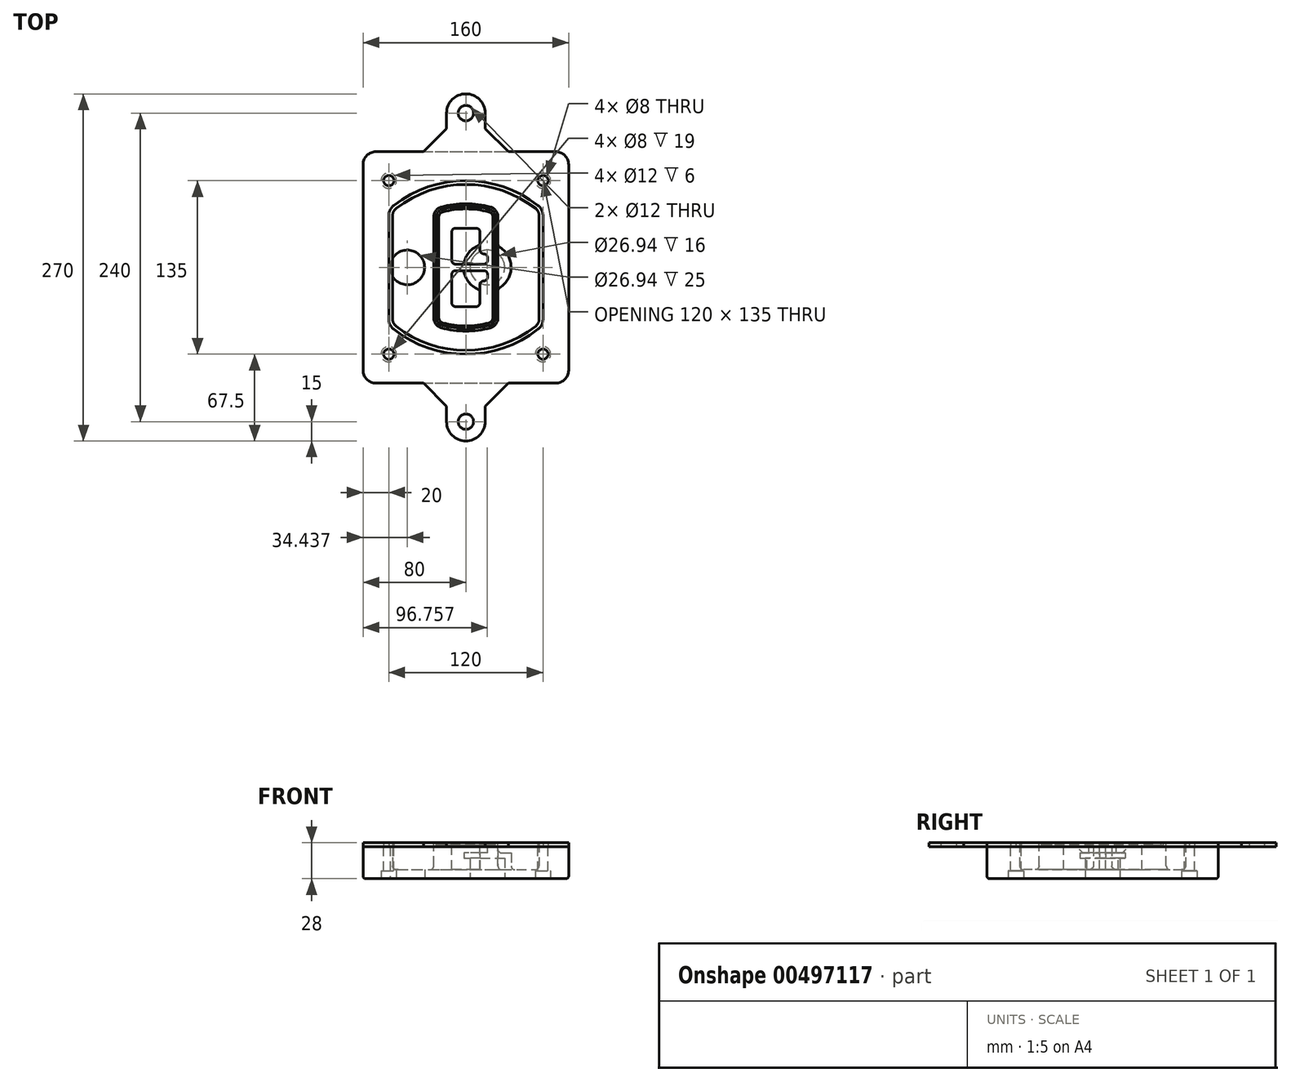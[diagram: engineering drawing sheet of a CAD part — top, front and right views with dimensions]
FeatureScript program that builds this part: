
annotation { "Feature Type Name" : "Feature", "Feature Type Description" : "" }
export const myFeature = defineFeature(function(context is Context, id is Id, definition is map)
    precondition{}
    {
        {
            var Q0;
            Q0=qCreatedBy(makeId("Top.planeOp"),FACE);
            var sketch = newSketch(context, id + "F0", { "sketchPlane" : qUnion([Q0])});
            skPoint(sketch, "E0.rect.middle", {"position": v(0, 0) * mm});
            skLineSegment(sketch, "E1.bottom", {"start": v(-70, -90) * mm, "end": v(70, -90) * mm});
            skLineSegment(sketch, "E1.top", {"start": v(-70, 90) * mm, "end": v(70, 90) * mm});
            skLineSegment(sketch, "E1.left", {"start": v(-80, -80) * mm, "end": v(-80, 80) * mm});
            skLineSegment(sketch, "E1.right", {"start": v(80, -80) * mm, "end": v(80, 80) * mm});
            skLineSegment(sketch, "E2", {"start": v(-80, 90) * mm, "end": v(80, -90) * mm, "construction": true});
            skLineSegment(sketch, "E3", {"start": v(80, 90) * mm, "end": v(-80, -90) * mm, "construction": true});
            skCircle(sketch, "E4", {"center": v(-60, 67.5) * mm, "radius": 4 * mm});
            skCircle(sketch, "E5", {"center": v(60, 67.5) * mm, "radius": 4 * mm});
            skCircle(sketch, "E6", {"center": v(60, -67.5) * mm, "radius": 4 * mm});
            skCircle(sketch, "E7", {"center": v(-60, -67.5) * mm, "radius": 4 * mm});
            skLineSegment(sketch, "E8", {"start": v(-60, 67.5) * mm, "end": v(60, 67.5) * mm, "construction": true});
            skLineSegment(sketch, "E9", {"start": v(60, 67.5) * mm, "end": v(60, -67.5) * mm, "construction": true});
            skLineSegment(sketch, "E10", {"start": v(60, -67.5) * mm, "end": v(-60, -67.5) * mm, "construction": true});
            skLineSegment(sketch, "E11", {"start": v(-60, -67.5) * mm, "end": v(-60, 67.5) * mm, "construction": true});
            skLineSegment(sketch, "E12", {"start": v(-60, 40.3) * mm, "end": v(-60, -40.3) * mm});
            skLineSegment(sketch, "E13", {"start": v(60, 40.3) * mm, "end": v(60, -40.3) * mm});
            skArc(sketch, "E14", {"start": v(56.15, 48.18) * mm, "mid": v(0, 67.5) * mm, "end": v(-56.15, 48.18) * mm});
            skArc(sketch, "E15", {"start": v(-56.15, -48.18) * mm, "mid": v(0, -67.5) * mm, "end": v(56.15, -48.18) * mm});
            skLineSegment(sketch, "E16", {"start": v(-60, 0) * mm, "end": v(60, 0) * mm, "construction": true});
            skPoint(sketch, "E17.visualSharp", {"position": v(-60, -45) * mm});
            skArc(sketch, "E17.filletArc", {"start": v(-60, -40.3) * mm, "mid": v(-58.99, -44.68) * mm, "end": v(-56.15, -48.18) * mm});
            skPoint(sketch, "E18.visualSharp", {"position": v(-60, 45) * mm});
            skArc(sketch, "E18.filletArc", {"start": v(-56.15, 48.18) * mm, "mid": v(-58.99, 44.68) * mm, "end": v(-60, 40.3) * mm});
            skPoint(sketch, "E19.visualSharp", {"position": v(60, 45) * mm});
            skArc(sketch, "E19.filletArc", {"start": v(60, 40.3) * mm, "mid": v(58.99, 44.68) * mm, "end": v(56.15, 48.18) * mm});
            skPoint(sketch, "E20.visualSharp", {"position": v(60, -45) * mm});
            skArc(sketch, "E20.filletArc", {"start": v(56.15, -48.18) * mm, "mid": v(58.99, -44.68) * mm, "end": v(60, -40.3) * mm});
            skPoint(sketch, "E21.visualSharp", {"position": v(-80, 90) * mm});
            skArc(sketch, "E21.filletArc", {"start": v(-70, 90) * mm, "mid": v(-77.07, 87.07) * mm, "end": v(-80, 80) * mm});
            skPoint(sketch, "E22.visualSharp", {"position": v(80, 90) * mm});
            skArc(sketch, "E22.filletArc", {"start": v(80, 80) * mm, "mid": v(77.07, 87.07) * mm, "end": v(70, 90) * mm});
            skPoint(sketch, "E23.visualSharp", {"position": v(80, -90) * mm});
            skArc(sketch, "E23.filletArc", {"start": v(70, -90) * mm, "mid": v(77.07, -87.07) * mm, "end": v(80, -80) * mm});
            skPoint(sketch, "E24.visualSharp", {"position": v(-80, -90) * mm});
            skArc(sketch, "E24.filletArc", {"start": v(-80, -80) * mm, "mid": v(-77.07, -87.07) * mm, "end": v(-70, -90) * mm});
            skArc(sketch, "E25.0", {"start": v(57, 40.3) * mm, "mid": v(56.3, 43.36) * mm, "end": v(54.3, 45.81) * mm});
            skLineSegment(sketch, "E25.1", {"start": v(57, 40.3) * mm, "end": v(57, -40.3) * mm});
            skArc(sketch, "E25.2", {"start": v(54.3, -45.81) * mm, "mid": v(56.3, -43.36) * mm, "end": v(57, -40.3) * mm});
            skArc(sketch, "E25.3", {"start": v(-54.3, -45.81) * mm, "mid": v(0, -64.5) * mm, "end": v(54.3, -45.81) * mm});
            skArc(sketch, "E25.4", {"start": v(-57, -40.3) * mm, "mid": v(-56.3, -43.36) * mm, "end": v(-54.3, -45.81) * mm});
            skArc(sketch, "E25.5", {"start": v(54.3, 45.81) * mm, "mid": v(0, 64.5) * mm, "end": v(-54.3, 45.81) * mm});
            skLineSegment(sketch, "E25.6", {"start": v(-57, 40.3) * mm, "end": v(-57, -40.3) * mm});
            skArc(sketch, "E25.7", {"start": v(-54.3, 45.81) * mm, "mid": v(-56.3, 43.36) * mm, "end": v(-57, 40.3) * mm});
            skArc(sketch, "E26.0", {"start": v(-58.62, 51.33) * mm, "mid": v(-62.58, 46.43) * mm, "end": v(-64, 40.3) * mm});
            skArc(sketch, "E26.1", {"start": v(58.62, 51.33) * mm, "mid": v(0, 71.5) * mm, "end": v(-58.62, 51.33) * mm});
            skArc(sketch, "E26.2", {"start": v(64, 40.3) * mm, "mid": v(62.58, 46.43) * mm, "end": v(58.62, 51.33) * mm});
            skLineSegment(sketch, "E26.3", {"start": v(64, 40.3) * mm, "end": v(64, -40.3) * mm});
            skArc(sketch, "E26.4", {"start": v(58.62, -51.33) * mm, "mid": v(62.58, -46.43) * mm, "end": v(64, -40.3) * mm});
            skLineSegment(sketch, "E26.5", {"start": v(-64, 40.3) * mm, "end": v(-64, -40.3) * mm});
            skArc(sketch, "E26.6", {"start": v(-58.62, -51.33) * mm, "mid": v(0, -71.5) * mm, "end": v(58.62, -51.33) * mm});
            skArc(sketch, "E26.7", {"start": v(-64, -40.3) * mm, "mid": v(-62.58, -46.43) * mm, "end": v(-58.62, -51.33) * mm});
            skSolve(sketch);
        }
        {
            var Q0;
            Q0=makeQuery(id+"F0.imprint","IMPRINT",FACE,{"disambiguationData":[TD([[makeQuery(id+"F0.imprint","IMPRINT",EDGE,{"derivedFrom":sQuery(id+"F0.wireOp",EDGE,"E1.bottom")}),1.0]])]});
            var Q1;
            Q1=makeQuery(id+"F0.imprint","IMPRINT",FACE,{"disambiguationData":[TD([[makeQuery(id+"F0.imprint","IMPRINT",EDGE,{"derivedFrom":sQuery(id+"F0.wireOp",EDGE,"E12")}),1.0]])]});
            var Q2;
            Q2=makeQuery(id+"F0.imprint","IMPRINT",FACE,{"disambiguationData":[TD([[makeQuery(id+"F0.imprint","IMPRINT",EDGE,{"derivedFrom":sQuery(id+"F0.wireOp",EDGE,"E25.0")}),1.0]])]});
            var Q3;
            Q3=makeQuery(id+"F0.imprint","IMPRINT",FACE,{"disambiguationData":[TD([[makeQuery(id+"F0.imprint","IMPRINT",EDGE,{"derivedFrom":sQuery(id+"F0.wireOp",EDGE,"E12")}),-1.0]])]});
            extrude(context, id + "F1", {"entities" : qUnion([Q0, Q1, Q2, Q3]), "oppositeDirection" : true, "depth" : 25 * mm});
        }
        {
            var Q0;
            Q0=makeQuery(id+"F0.imprint","IMPRINT",FACE,{"disambiguationData":[TD([[makeQuery(id+"F0.imprint","IMPRINT",EDGE,{"derivedFrom":sQuery(id+"F0.wireOp",EDGE,"E12")}),1.0]])]});
            extrude(context, id + "F2", {"entities" : qUnion([Q0]), "operationType" : NewBodyOperationType.ADD, "depth" : 3 * mm});
        }
        {
            var Q0;
            Q0=makeQuery(id+"F0.imprint","IMPRINT",FACE,{"disambiguationData":[TD([[makeQuery(id+"F0.imprint","IMPRINT",EDGE,{"derivedFrom":sQuery(id+"F0.wireOp",EDGE,"E25.0")}),1.0]])]});
            extrude(context, id + "F3", {"entities" : qUnion([Q0]), "operationType" : NewBodyOperationType.REMOVE, "oppositeDirection" : true, "depth" : 18 * mm});
        }
        {
            var Q0;
            Q0=makeQuery(id+"F2.opExtrude","CAP_FACE",FACE,{"disambiguationData":[OSD([sQuery(id+"F0.wireOp",EDGE,"E12"),sQuery(id+"F0.wireOp",EDGE,"E13"),sQuery(id+"F0.wireOp",EDGE,"E14"),sQuery(id+"F0.wireOp",EDGE,"E15"),sQuery(id+"F0.wireOp",EDGE,"E17.filletArc"),sQuery(id+"F0.wireOp",EDGE,"E18.filletArc"),sQuery(id+"F0.wireOp",EDGE,"E19.filletArc"),sQuery(id+"F0.wireOp",EDGE,"E20.filletArc"),sQuery(id+"F0.wireOp",EDGE,"E25.0"),sQuery(id+"F0.wireOp",EDGE,"E25.1"),sQuery(id+"F0.wireOp",EDGE,"E25.2"),sQuery(id+"F0.wireOp",EDGE,"E25.3"),sQuery(id+"F0.wireOp",EDGE,"E25.4"),sQuery(id+"F0.wireOp",EDGE,"E25.5"),sQuery(id+"F0.wireOp",EDGE,"E25.6"),sQuery(id+"F0.wireOp",EDGE,"E25.7")])],"isStart":false});
            var sketch = newSketch(context, id + "F4", { "sketchPlane" : qUnion([Q0])});
            skArc(sketch, "E27.0", {"start": v(-19.08, -46.97) * mm, "mid": v(0, -49.5) * mm, "end": v(19.08, -46.97) * mm});
            skArc(sketch, "E28.0", {"start": v(19.08, 46.97) * mm, "mid": v(0, 49.5) * mm, "end": v(-19.08, 46.97) * mm});
            skLineSegment(sketch, "E29", {"start": v(-25, 39.25) * mm, "end": v(-25, -39.25) * mm});
            skLineSegment(sketch, "E30", {"start": v(25, 39.25) * mm, "end": v(25, -39.25) * mm});
            skLineSegment(sketch, "E31", {"start": v(-25, 45.1) * mm, "end": v(25, 45.1) * mm, "construction": true});
            skLineSegment(sketch, "E32", {"start": v(-25, -45.1) * mm, "end": v(25, -45.1) * mm, "construction": true});
            skPoint(sketch, "E33.visualSharp", {"position": v(-25, 45.1) * mm});
            skArc(sketch, "E33.filletArc", {"start": v(-19.08, 46.97) * mm, "mid": v(-23.35, 44.11) * mm, "end": v(-25, 39.25) * mm});
            skPoint(sketch, "E34.visualSharp", {"position": v(25, 45.1) * mm});
            skArc(sketch, "E34.filletArc", {"start": v(25, 39.25) * mm, "mid": v(23.35, 44.11) * mm, "end": v(19.08, 46.97) * mm});
            skPoint(sketch, "E35.visualSharp", {"position": v(25, -45.1) * mm});
            skArc(sketch, "E35.filletArc", {"start": v(19.08, -46.97) * mm, "mid": v(23.35, -44.11) * mm, "end": v(25, -39.25) * mm});
            skPoint(sketch, "E36.visualSharp", {"position": v(-25, -45.1) * mm});
            skArc(sketch, "E36.filletArc", {"start": v(-25, -39.25) * mm, "mid": v(-23.35, -44.11) * mm, "end": v(-19.08, -46.97) * mm});
            skArc(sketch, "E37.0", {"start": v(54.3, 45.81) * mm, "mid": v(0, 64.5) * mm, "end": v(-54.3, 45.81) * mm});
            skArc(sketch, "E37.1", {"start": v(-54.3, 45.81) * mm, "mid": v(-56.3, 43.36) * mm, "end": v(-57, 40.3) * mm});
            skLineSegment(sketch, "E37.2", {"start": v(-57, 40.3) * mm, "end": v(-57, -40.3) * mm});
            skArc(sketch, "E37.3", {"start": v(-57, -40.3) * mm, "mid": v(-56.3, -43.36) * mm, "end": v(-54.3, -45.81) * mm});
            skArc(sketch, "E37.4", {"start": v(-54.3, -45.81) * mm, "mid": v(0, -64.5) * mm, "end": v(54.3, -45.81) * mm});
            skArc(sketch, "E37.5", {"start": v(54.3, -45.81) * mm, "mid": v(56.3, -43.36) * mm, "end": v(57, -40.3) * mm});
            skLineSegment(sketch, "E37.6", {"start": v(57, 40.3) * mm, "end": v(57, -40.3) * mm});
            skArc(sketch, "E37.7", {"start": v(57, 40.3) * mm, "mid": v(56.3, 43.36) * mm, "end": v(54.3, 45.81) * mm});
            skLineSegment(sketch, "E38.0", {"start": v(23, 39.25) * mm, "end": v(23, -39.25) * mm});
            skArc(sketch, "E38.1", {"start": v(18.56, -45.04) * mm, "mid": v(21.76, -42.9) * mm, "end": v(23, -39.25) * mm});
            skArc(sketch, "E38.2", {"start": v(-18.56, -45.04) * mm, "mid": v(0, -47.5) * mm, "end": v(18.56, -45.04) * mm});
            skArc(sketch, "E38.3", {"start": v(-23, -39.25) * mm, "mid": v(-21.76, -42.9) * mm, "end": v(-18.56, -45.04) * mm});
            skLineSegment(sketch, "E38.4", {"start": v(-23, 39.25) * mm, "end": v(-23, -39.25) * mm});
            skArc(sketch, "E38.5", {"start": v(23, 39.25) * mm, "mid": v(21.76, 42.9) * mm, "end": v(18.56, 45.04) * mm});
            skArc(sketch, "E38.6", {"start": v(-18.56, 45.04) * mm, "mid": v(-21.76, 42.9) * mm, "end": v(-23, 39.25) * mm});
            skArc(sketch, "E38.7", {"start": v(18.56, 45.04) * mm, "mid": v(0, 47.5) * mm, "end": v(-18.56, 45.04) * mm});
            skArc(sketch, "E39.0", {"start": v(21, 39.25) * mm, "mid": v(20.18, 41.68) * mm, "end": v(18.04, 43.1) * mm});
            skLineSegment(sketch, "E39.1", {"start": v(21, 39.25) * mm, "end": v(21, -39.25) * mm});
            skArc(sketch, "E39.2", {"start": v(18.04, -43.1) * mm, "mid": v(20.18, -41.68) * mm, "end": v(21, -39.25) * mm});
            skArc(sketch, "E39.3", {"start": v(-18.04, -43.1) * mm, "mid": v(0, -45.5) * mm, "end": v(18.04, -43.1) * mm});
            skArc(sketch, "E39.4", {"start": v(-21, -39.25) * mm, "mid": v(-20.18, -41.68) * mm, "end": v(-18.04, -43.1) * mm});
            skArc(sketch, "E39.5", {"start": v(18.04, 43.1) * mm, "mid": v(0, 45.5) * mm, "end": v(-18.04, 43.1) * mm});
            skLineSegment(sketch, "E39.6", {"start": v(-21, 39.25) * mm, "end": v(-21, -39.25) * mm});
            skArc(sketch, "E39.7", {"start": v(-18.04, 43.1) * mm, "mid": v(-20.18, 41.68) * mm, "end": v(-21, 39.25) * mm});
            skLineSegment(sketch, "E40", {"start": v(-25, 0) * mm, "end": v(25, 0) * mm, "construction": true});
            skLineSegment(sketch, "E41", {"start": v(-11, 5.5) * mm, "end": v(-11, 27.5) * mm});
            skLineSegment(sketch, "E42", {"start": v(-8, 30.5) * mm, "end": v(8, 30.5) * mm});
            skLineSegment(sketch, "E43", {"start": v(11, 27.5) * mm, "end": v(11, 13.5) * mm});
            skLineSegment(sketch, "E44", {"start": v(14, 10.5) * mm, "end": v(14, 10.5) * mm});
            skLineSegment(sketch, "E45", {"start": v(17, 7.5) * mm, "end": v(17, 5.5) * mm});
            skLineSegment(sketch, "E46", {"start": v(14, 2.5) * mm, "end": v(-8, 2.5) * mm});
            skPoint(sketch, "E47.visualSharp", {"position": v(-11, 30.5) * mm});
            skArc(sketch, "E47.filletArc", {"start": v(-8, 30.5) * mm, "mid": v(-10.12, 29.62) * mm, "end": v(-11, 27.5) * mm});
            skPoint(sketch, "E48.visualSharp", {"position": v(11, 30.5) * mm});
            skArc(sketch, "E48.filletArc", {"start": v(11, 27.5) * mm, "mid": v(10.12, 29.62) * mm, "end": v(8, 30.5) * mm});
            skPoint(sketch, "E49.visualSharp", {"position": v(11, 10.5) * mm});
            skArc(sketch, "E49.filletArc", {"start": v(11, 13.5) * mm, "mid": v(11.88, 11.38) * mm, "end": v(14, 10.5) * mm});
            skPoint(sketch, "E50.visualSharp", {"position": v(17, 10.5) * mm});
            skArc(sketch, "E50.filletArc", {"start": v(17, 7.5) * mm, "mid": v(16.12, 9.62) * mm, "end": v(14, 10.5) * mm});
            skPoint(sketch, "E51.visualSharp", {"position": v(17, 2.5) * mm});
            skArc(sketch, "E51.filletArc", {"start": v(14, 2.5) * mm, "mid": v(16.12, 3.38) * mm, "end": v(17, 5.5) * mm});
            skPoint(sketch, "E52.visualSharp", {"position": v(-11, 2.5) * mm});
            skArc(sketch, "E52.filletArc", {"start": v(-11, 5.5) * mm, "mid": v(-10.12, 3.38) * mm, "end": v(-8, 2.5) * mm});
            skLineSegment(sketch, "E53.0.MirrorCS", {"start": v(14, -2.5) * mm, "end": v(-8, -2.5) * mm});
            skArc(sketch, "E54.0.MirrorCS", {"start": v(-11, -5.5) * mm, "mid": v(-10.12, -3.38) * mm, "end": v(-8, -2.5) * mm});
            skLineSegment(sketch, "E55.0.MirrorCS", {"start": v(-11, -5.5) * mm, "end": v(-11, -27.5) * mm});
            skArc(sketch, "E56.0.MirrorCS", {"start": v(-8, -30.5) * mm, "mid": v(-10.12, -29.62) * mm, "end": v(-11, -27.5) * mm});
            skLineSegment(sketch, "E57.0.MirrorCS", {"start": v(-8, -30.5) * mm, "end": v(8, -30.5) * mm});
            skArc(sketch, "E58.0.MirrorCS", {"start": v(11, -27.5) * mm, "mid": v(10.12, -29.62) * mm, "end": v(8, -30.5) * mm});
            skLineSegment(sketch, "E59.0.MirrorCS", {"start": v(11, -27.5) * mm, "end": v(11, -13.5) * mm});
            skArc(sketch, "E60.0.MirrorCS", {"start": v(11, -13.5) * mm, "mid": v(11.88, -11.38) * mm, "end": v(14, -10.5) * mm});
            skArc(sketch, "E61.0.MirrorCS", {"start": v(17, -7.5) * mm, "mid": v(16.12, -9.62) * mm, "end": v(14, -10.5) * mm});
            skLineSegment(sketch, "E62.0.MirrorCS", {"start": v(17, -7.5) * mm, "end": v(17, -5.5) * mm});
            skArc(sketch, "E63.0.MirrorCS", {"start": v(14, -2.5) * mm, "mid": v(16.12, -3.38) * mm, "end": v(17, -5.5) * mm});
            skSolve(sketch);
        }
        {
            var Q0;
            Q0=makeQuery(id+"F4.imprint","IMPRINT",FACE,{"disambiguationData":[TD([[makeQuery(id+"F4.imprint","IMPRINT",EDGE,{"derivedFrom":sQuery(id+"F4.wireOp",EDGE,"E27.0")}),1.0]])]});
            var Q1;
            Q1=makeQuery(id+"F4.imprint","IMPRINT",FACE,{"disambiguationData":[TD([[makeQuery(id+"F4.imprint","IMPRINT",EDGE,{"derivedFrom":sQuery(id+"F4.wireOp",EDGE,"E38.0")}),-1.0]])]});
            var Q2;
            Q2=makeQuery(id+"F4.imprint","IMPRINT",FACE,{"disambiguationData":[TD([[makeQuery(id+"F4.imprint","IMPRINT",EDGE,{"derivedFrom":sQuery(id+"F4.wireOp",EDGE,"E39.0")}),1.0]])]});
            extrude(context, id + "F5", {"entities" : qUnion([Q0, Q1, Q2]), "operationType" : NewBodyOperationType.ADD, "endBound" : BoundingType.UP_TO_NEXT, "oppositeDirection" : true, "depth" : 25 * mm});
        }
        {
            var Q0;
            Q0=makeQuery(id+"F4.imprint","IMPRINT",FACE,{"disambiguationData":[TD([[makeQuery(id+"F4.imprint","IMPRINT",EDGE,{"derivedFrom":sQuery(id+"F4.wireOp",EDGE,"E38.0")}),-1.0]])]});
            extrude(context, id + "F6", {"entities" : qUnion([Q0]), "operationType" : NewBodyOperationType.REMOVE, "oppositeDirection" : true, "depth" : 2 * mm});
        }
        {
            var Q0;
            Q0=makeQuery(id+"F1.opExtrude","CAP_FACE",FACE,{"disambiguationData":[OSD([sQuery(id+"F0.wireOp",EDGE,"E1.bottom"),sQuery(id+"F0.wireOp",EDGE,"E1.top"),sQuery(id+"F0.wireOp",EDGE,"E1.left"),sQuery(id+"F0.wireOp",EDGE,"E1.right"),sQuery(id+"F0.wireOp",EDGE,"E4"),sQuery(id+"F0.wireOp",EDGE,"E5"),sQuery(id+"F0.wireOp",EDGE,"E6"),sQuery(id+"F0.wireOp",EDGE,"E7"),sQuery(id+"F0.wireOp",EDGE,"E21.filletArc"),sQuery(id+"F0.wireOp",EDGE,"E22.filletArc"),sQuery(id+"F0.wireOp",EDGE,"E23.filletArc"),sQuery(id+"F0.wireOp",EDGE,"E24.filletArc")])],"isStart":false});
            var sketch = newSketch(context, id + "F7", { "sketchPlane" : qUnion([Q0])});
            skCircle(sketch, "E64", {"center": v(16.76, 0) * mm, "radius": 13.47 * mm});
            skCircle(sketch, "E65", {"center": v(-45.56, 0) * mm, "radius": 13.47 * mm});
            skLineSegment(sketch, "E66", {"start": v(80, 0) * mm, "end": v(-80, 0) * mm});
            skCircle(sketch, "E67", {"center": v(16.76, 0) * mm, "radius": 18.47 * mm});
            skCircle(sketch, "E68", {"center": v(60, -67.5) * mm, "radius": 6 * mm});
            skCircle(sketch, "E69", {"center": v(-60, -67.5) * mm, "radius": 6 * mm});
            skCircle(sketch, "E70", {"center": v(-60, 67.5) * mm, "radius": 6 * mm});
            skCircle(sketch, "E71", {"center": v(60, 67.5) * mm, "radius": 6 * mm});
            skSolve(sketch);
        }
        {
            var Q0;
            {var subQ1=sQuery(id+"F7.wireOp",EDGE,"E66");var subQ4=sQuery(id+"F7.wireOp",EDGE,"E64");var subQ6=makeQuery(id+"F7.imprint","INTERSECT",VERTEX,{"disambiguationData":[OD(0.0)],"derivedFrom":[subQ4,subQ1]});Q0=makeQuery(id+"F7.imprint","IMPRINT",FACE,{"disambiguationData":[TD([[makeQuery(id+"F7.imprint","IMPRINT",EDGE,{"disambiguationData":[TD([[subQ6,-1.0]])],"derivedFrom":subQ4}),-1.0]])]});}
            var Q1;
            {var subQ0=sQuery(id+"F7.wireOp",EDGE,"E66");var subQ1=sQuery(id+"F7.wireOp",EDGE,"E64");var subQ3=makeQuery(id+"F7.imprint","INTERSECT",VERTEX,{"disambiguationData":[OD(0.0)],"derivedFrom":[subQ1,subQ0]});Q1=makeQuery(id+"F7.imprint","IMPRINT",FACE,{"disambiguationData":[TD([[makeQuery(id+"F7.imprint","IMPRINT",EDGE,{"disambiguationData":[TD([[subQ3,-1.0]])],"derivedFrom":subQ1}),1.0]])]});}
            var Q2;
            {var subQ0=sQuery(id+"F7.wireOp",EDGE,"E66");var subQ1=sQuery(id+"F7.wireOp",EDGE,"E64");var subQ3=makeQuery(id+"F7.imprint","INTERSECT",VERTEX,{"disambiguationData":[OD(0.0)],"derivedFrom":[subQ1,subQ0]});Q2=makeQuery(id+"F7.imprint","IMPRINT",FACE,{"disambiguationData":[TD([[makeQuery(id+"F7.imprint","IMPRINT",EDGE,{"disambiguationData":[TD([[subQ3,1.0]])],"derivedFrom":subQ1}),1.0]])]});}
            var Q3;
            {var subQ1=sQuery(id+"F7.wireOp",EDGE,"E66");var subQ4=sQuery(id+"F7.wireOp",EDGE,"E64");var subQ6=makeQuery(id+"F7.imprint","INTERSECT",VERTEX,{"disambiguationData":[OD(0.0)],"derivedFrom":[subQ4,subQ1]});Q3=makeQuery(id+"F7.imprint","IMPRINT",FACE,{"disambiguationData":[TD([[makeQuery(id+"F7.imprint","IMPRINT",EDGE,{"disambiguationData":[TD([[subQ6,1.0]])],"derivedFrom":subQ4}),-1.0]])]});}
            extrude(context, id + "F8", {"entities" : qUnion([Q0, Q1, Q2, Q3]), "operationType" : NewBodyOperationType.ADD, "oppositeDirection" : true, "depth" : 20 * mm});
        }
        {
            var Q0;
            {var subQ0=sQuery(id+"F7.wireOp",EDGE,"E66");var subQ1=sQuery(id+"F7.wireOp",EDGE,"E64");var subQ3=makeQuery(id+"F7.imprint","INTERSECT",VERTEX,{"disambiguationData":[OD(0.0)],"derivedFrom":[subQ1,subQ0]});Q0=makeQuery(id+"F7.imprint","IMPRINT",FACE,{"disambiguationData":[TD([[makeQuery(id+"F7.imprint","IMPRINT",EDGE,{"disambiguationData":[TD([[subQ3,-1.0]])],"derivedFrom":subQ1}),1.0]])]});}
            var Q1;
            {var subQ0=sQuery(id+"F7.wireOp",EDGE,"E66");var subQ1=sQuery(id+"F7.wireOp",EDGE,"E64");var subQ3=makeQuery(id+"F7.imprint","INTERSECT",VERTEX,{"disambiguationData":[OD(0.0)],"derivedFrom":[subQ1,subQ0]});Q1=makeQuery(id+"F7.imprint","IMPRINT",FACE,{"disambiguationData":[TD([[makeQuery(id+"F7.imprint","IMPRINT",EDGE,{"disambiguationData":[TD([[subQ3,1.0]])],"derivedFrom":subQ1}),1.0]])]});}
            extrude(context, id + "F9", {"entities" : qUnion([Q0, Q1]), "operationType" : NewBodyOperationType.REMOVE, "oppositeDirection" : true, "depth" : 16 * mm});
        }
        {
            var Q0;
            {var subQ0=sQuery(id+"F7.wireOp",EDGE,"E66");var subQ1=sQuery(id+"F7.wireOp",EDGE,"E65");var subQ3=makeQuery(id+"F7.imprint","INTERSECT",VERTEX,{"disambiguationData":[OD(0.0)],"derivedFrom":[subQ1,subQ0]});Q0=makeQuery(id+"F7.imprint","IMPRINT",FACE,{"disambiguationData":[TD([[makeQuery(id+"F7.imprint","IMPRINT",EDGE,{"disambiguationData":[TD([[subQ3,-1.0]])],"derivedFrom":subQ1}),1.0]])]});}
            var Q1;
            {var subQ0=sQuery(id+"F7.wireOp",EDGE,"E66");var subQ1=sQuery(id+"F7.wireOp",EDGE,"E65");var subQ3=makeQuery(id+"F7.imprint","INTERSECT",VERTEX,{"disambiguationData":[OD(0.0)],"derivedFrom":[subQ1,subQ0]});Q1=makeQuery(id+"F7.imprint","IMPRINT",FACE,{"disambiguationData":[TD([[makeQuery(id+"F7.imprint","IMPRINT",EDGE,{"disambiguationData":[TD([[subQ3,1.0]])],"derivedFrom":subQ1}),1.0]])]});}
            extrude(context, id + "F10", {"entities" : qUnion([Q0, Q1]), "operationType" : NewBodyOperationType.REMOVE, "oppositeDirection" : true, "depth" : 25 * mm});
        }
        {
            var Q0;
            Q0=makeQuery(id+"F7.imprint","IMPRINT",FACE,{"disambiguationData":[TD([[makeQuery(id+"F7.imprint","IMPRINT",EDGE,{"derivedFrom":sQuery(id+"F7.wireOp",EDGE,"E68")}),1.0]])]});
            var Q1;
            Q1=makeQuery(id+"F7.imprint","IMPRINT",FACE,{"disambiguationData":[TD([[makeQuery(id+"F7.imprint","IMPRINT",EDGE,{"derivedFrom":makeQuery(id+"F1.opExtrude","CAP_EDGE",EDGE,{"disambiguationData":[OSD([sQuery(id+"F0.wireOp",EDGE,"E5")])],"isStart":false})}),-1.0]])]});
            var Q2;
            Q2=makeQuery(id+"F7.imprint","IMPRINT",FACE,{"disambiguationData":[TD([[makeQuery(id+"F7.imprint","IMPRINT",EDGE,{"derivedFrom":sQuery(id+"F7.wireOp",EDGE,"E69")}),1.0]])]});
            var Q3;
            Q3=makeQuery(id+"F7.imprint","IMPRINT",FACE,{"disambiguationData":[TD([[makeQuery(id+"F7.imprint","IMPRINT",EDGE,{"derivedFrom":makeQuery(id+"F1.opExtrude","CAP_EDGE",EDGE,{"disambiguationData":[OSD([sQuery(id+"F0.wireOp",EDGE,"E4")])],"isStart":false})}),-1.0]])]});
            var Q4;
            Q4=makeQuery(id+"F7.imprint","IMPRINT",FACE,{"disambiguationData":[TD([[makeQuery(id+"F7.imprint","IMPRINT",EDGE,{"derivedFrom":sQuery(id+"F7.wireOp",EDGE,"E70")}),1.0]])]});
            var Q5;
            Q5=makeQuery(id+"F7.imprint","IMPRINT",FACE,{"disambiguationData":[TD([[makeQuery(id+"F7.imprint","IMPRINT",EDGE,{"derivedFrom":makeQuery(id+"F1.opExtrude","CAP_EDGE",EDGE,{"disambiguationData":[OSD([sQuery(id+"F0.wireOp",EDGE,"E7")])],"isStart":false})}),-1.0]])]});
            var Q6;
            Q6=makeQuery(id+"F7.imprint","IMPRINT",FACE,{"disambiguationData":[TD([[makeQuery(id+"F7.imprint","IMPRINT",EDGE,{"derivedFrom":sQuery(id+"F7.wireOp",EDGE,"E71")}),1.0]])]});
            var Q7;
            Q7=makeQuery(id+"F7.imprint","IMPRINT",FACE,{"disambiguationData":[TD([[makeQuery(id+"F7.imprint","IMPRINT",EDGE,{"derivedFrom":makeQuery(id+"F1.opExtrude","CAP_EDGE",EDGE,{"disambiguationData":[OSD([sQuery(id+"F0.wireOp",EDGE,"E6")])],"isStart":false})}),-1.0]])]});
            extrude(context, id + "F11", {"entities" : qUnion([Q0, Q1, Q2, Q3, Q4, Q5, Q6, Q7]), "operationType" : NewBodyOperationType.REMOVE, "oppositeDirection" : true, "depth" : 6 * mm});
        }
        {
            var Q0;
            Q0=makeQuery(id+"F9.boolean.opBoolean","COPY",FACE,{"derivedFrom":makeQuery(id+"F9.opExtrude","CAP_FACE",FACE,{"disambiguationData":[OSD([sQuery(id+"F7.wireOp",EDGE,"E64")])],"isStart":false})});
            var sketch = newSketch(context, id + "F12", { "sketchPlane" : qUnion([Q0])});
            skArc(sketch, "E72.0", {"start": v(11, 17.55) * mm, "mid": v(2.57, 11.82) * mm, "end": v(-1.54, 2.5) * mm});
            skArc(sketch, "E72.1", {"start": v(-1.54, -2.5) * mm, "mid": v(2.57, -11.82) * mm, "end": v(11, -17.55) * mm});
            skLineSegment(sketch, "E73", {"start": v(-1.54, -2.5) * mm, "end": v(14, -2.5) * mm});
            skLineSegment(sketch, "E74.0", {"start": v(14, 2.5) * mm, "end": v(-1.54, 2.5) * mm});
            skArc(sketch, "E74.1", {"start": v(14, 2.5) * mm, "mid": v(16.12, 3.38) * mm, "end": v(17, 5.5) * mm});
            skLineSegment(sketch, "E74.2", {"start": v(17, 7.5) * mm, "end": v(17, 5.5) * mm});
            skArc(sketch, "E74.3", {"start": v(17, 7.5) * mm, "mid": v(16.12, 9.62) * mm, "end": v(14, 10.5) * mm});
            skArc(sketch, "E74.4", {"start": v(11, 13.5) * mm, "mid": v(11.88, 11.38) * mm, "end": v(14, 10.5) * mm});
            skLineSegment(sketch, "E74.5", {"start": v(11, 17.55) * mm, "end": v(11, 13.5) * mm});
            skLineSegment(sketch, "E74.7", {"start": v(14, -2.5) * mm, "end": v(-1.54, -2.5) * mm});
            skArc(sketch, "E74.8", {"start": v(14, -2.5) * mm, "mid": v(16.12, -3.38) * mm, "end": v(17, -5.5) * mm});
            skLineSegment(sketch, "E74.9", {"start": v(17, -7.5) * mm, "end": v(17, -5.5) * mm});
            skArc(sketch, "E74.10", {"start": v(17, -7.5) * mm, "mid": v(16.12, -9.62) * mm, "end": v(14, -10.5) * mm});
            skArc(sketch, "E74.11", {"start": v(11, -13.5) * mm, "mid": v(11.88, -11.38) * mm, "end": v(14, -10.5) * mm});
            skLineSegment(sketch, "E74.12", {"start": v(11, -17.55) * mm, "end": v(11, -13.5) * mm});
            skPoint(sketch, "E75.orphan", {"position": v(11, -27.5) * mm});
            skPoint(sketch, "E76.orphan", {"position": v(-8, -2.5) * mm});
            skPoint(sketch, "E77.orphan", {"position": v(-8, 2.5) * mm});
            skPoint(sketch, "E78.orphan", {"position": v(11, 27.5) * mm});
            skSolve(sketch);
        }
        {
            var Q0;
            {var subQ7=sQuery(id+"F12.wireOp",EDGE,"E72.0");var subQ14=sQuery(id+"F12.wireOp",EDGE,"E72.1");var subQ16=sQuery(id+"F12.wireOp",EDGE,"E74.1");var subQ18=sQuery(id+"F12.wireOp",EDGE,"E74.8");Q0=qUnion([makeQuery(id+"F12.imprint","IMPRINT",FACE,{"disambiguationData":[TD([[makeQuery(id+"F12.imprint","IMPRINT",EDGE,{"derivedFrom":subQ7}),1.0]])]}),makeQuery(id+"F12.imprint","IMPRINT",FACE,{"disambiguationData":[TD([[makeQuery(id+"F12.imprint","IMPRINT",EDGE,{"derivedFrom":subQ14}),1.0]])]}),makeQuery(id+"F12.imprint","IMPRINT",FACE,{"disambiguationData":[TD([[makeQuery(id+"F12.imprint","IMPRINT",EDGE,{"derivedFrom":subQ16}),1.0]])]}),makeQuery(id+"F12.imprint","IMPRINT",FACE,{"disambiguationData":[TD([[makeQuery(id+"F12.imprint","IMPRINT",EDGE,{"derivedFrom":subQ18}),-1.0]])]})]);}
            var Q1;
            Q1=makeQuery(id+"F5.boolean.opBoolean","SPLIT",FACE,{"disambiguationData":[TD([makeQuery(id+"F5.opExtrude","SWEPT_FACE",FACE,{"disambiguationData":[OSD([sQuery(id+"F4.wireOp",EDGE,"E41")])]})])],"derivedFrom":makeQuery(id+"F3.boolean.opBoolean","COPY",FACE,{"derivedFrom":makeQuery(id+"F3.opExtrude","CAP_FACE",FACE,{"disambiguationData":[OSD([sQuery(id+"F0.wireOp",EDGE,"E25.0"),sQuery(id+"F0.wireOp",EDGE,"E25.1"),sQuery(id+"F0.wireOp",EDGE,"E25.2"),sQuery(id+"F0.wireOp",EDGE,"E25.3"),sQuery(id+"F0.wireOp",EDGE,"E25.4"),sQuery(id+"F0.wireOp",EDGE,"E25.5"),sQuery(id+"F0.wireOp",EDGE,"E25.6"),sQuery(id+"F0.wireOp",EDGE,"E25.7")])],"isStart":false})})});
            extrude(context, id + "F13", {"entities" : qUnion([Q0]), "operationType" : NewBodyOperationType.REMOVE, "endBound" : BoundingType.UP_TO_SURFACE, "endBoundEntityFace" : qUnion([Q1]), "depth" : 25 * mm});
        }
        {
            var Q0;
            Q0=makeQuery(id+"F3.boolean.opBoolean","COPY",EDGE,{"derivedFrom":makeQuery(id+"F3.opExtrude","CAP_EDGE",EDGE,{"disambiguationData":[OSD([sQuery(id+"F0.wireOp",EDGE,"E25.6")])],"isStart":false})});
            var Q1;
            Q1=makeQuery(id+"F8.boolean.opBoolean","INTERSECT",EDGE,{"derivedFrom":[makeQuery(id+"F5.opExtrude","SWEPT_FACE",FACE,{"disambiguationData":[OSD([sQuery(id+"F4.wireOp",EDGE,"E30")])]}),makeQuery(id+"F8.opExtrude","CAP_FACE",FACE,{"disambiguationData":[OSD([sQuery(id+"F7.wireOp",EDGE,"E67")])],"isStart":false})]});
            var Q2;
            Q2=makeQuery(id+"F8.boolean.opBoolean","INTERSECT",EDGE,{"disambiguationData":[OD(1.0)],"derivedFrom":[makeQuery(id+"F5.opExtrude","SWEPT_FACE",FACE,{"disambiguationData":[OSD([sQuery(id+"F4.wireOp",EDGE,"E30")])]}),makeQuery(id+"F8.opExtrude","SWEPT_FACE",FACE,{"disambiguationData":[OSD([sQuery(id+"F7.wireOp",EDGE,"E67")])]})]});
            var Q3;
            {var subQ0=sQuery(id+"F4.wireOp",EDGE,"E30");Q3=makeQuery(id+"F8.boolean.opBoolean","SPLIT",EDGE,{"disambiguationData":[TD([makeQuery(id+"F5.opExtrude","SWEPT_FACE",FACE,{"disambiguationData":[OSD([sQuery(id+"F4.wireOp",EDGE,"E35.filletArc")])]})])],"derivedFrom":makeQuery(id+"F5.opExtrude","CAP_EDGE",EDGE,{"disambiguationData":[OSD([subQ0])],"isStart":false})});}
            var Q4;
            {var subQ0=sQuery(id+"F0.wireOp",EDGE,"E25.7");var subQ1=sQuery(id+"F0.wireOp",EDGE,"E25.1");var subQ2=sQuery(id+"F0.wireOp",EDGE,"E25.6");var subQ3=sQuery(id+"F0.wireOp",EDGE,"E25.5");var subQ4=sQuery(id+"F0.wireOp",EDGE,"E25.4");var subQ5=sQuery(id+"F0.wireOp",EDGE,"E25.0");var subQ6=sQuery(id+"F0.wireOp",EDGE,"E25.2");var subQ7=sQuery(id+"F0.wireOp",EDGE,"E25.3");Q4=makeQuery(id+"F8.boolean.opBoolean","INTERSECT",EDGE,{"derivedFrom":[makeQuery(id+"F5.boolean.opBoolean","SPLIT",FACE,{"disambiguationData":[TD([makeQuery(id+"F2.opExtrude","SWEPT_FACE",FACE,{"disambiguationData":[OSD([subQ5])]})])],"derivedFrom":makeQuery(id+"F3.boolean.opBoolean","COPY",FACE,{"derivedFrom":makeQuery(id+"F3.opExtrude","CAP_FACE",FACE,{"disambiguationData":[OSD([subQ5,subQ1,subQ6,subQ7,subQ4,subQ3,subQ2,subQ0])],"isStart":false})})}),makeQuery(id+"F8.opExtrude","SWEPT_FACE",FACE,{"disambiguationData":[OSD([sQuery(id+"F7.wireOp",EDGE,"E67")])]})]});}
            var Q5;
            Q5=makeQuery(id+"F8.boolean.opBoolean","INTERSECT",EDGE,{"disambiguationData":[OD(0.0)],"derivedFrom":[makeQuery(id+"F5.opExtrude","SWEPT_FACE",FACE,{"disambiguationData":[OSD([sQuery(id+"F4.wireOp",EDGE,"E30")])]}),makeQuery(id+"F8.opExtrude","SWEPT_FACE",FACE,{"disambiguationData":[OSD([sQuery(id+"F7.wireOp",EDGE,"E67")])]})]});
            fillet(context, id + "F14", {"entities" : qUnion([Q0, Q1, Q2, Q3, Q4, Q5]), "radius" : 3 * mm, "tangentPropagation" : true, "allowEdgeOverflow" : false});
        }
        {
            var Q0;
            Q0=makeQuery(id+"F1.opExtrude","CAP_EDGE",EDGE,{"disambiguationData":[OSD([sQuery(id+"F0.wireOp",EDGE,"E1.bottom")])],"isStart":false});
            fillet(context, id + "F15", {"entities" : qUnion([Q0]), "radius" : 2 * mm, "tangentPropagation" : true, "allowEdgeOverflow" : false});
        }
        {
            var Q0;
            {var subQ0=sQuery(id+"F0.wireOp",EDGE,"E21.filletArc");var subQ1=sQuery(id+"F0.wireOp",EDGE,"E7");var subQ2=sQuery(id+"F0.wireOp",EDGE,"E6");var subQ3=sQuery(id+"F0.wireOp",EDGE,"E5");var subQ4=sQuery(id+"F0.wireOp",EDGE,"E4");var subQ5=sQuery(id+"F0.wireOp",EDGE,"E22.filletArc");var subQ6=sQuery(id+"F0.wireOp",EDGE,"E1.bottom");var subQ7=sQuery(id+"F0.wireOp",EDGE,"E1.right");var subQ8=sQuery(id+"F0.wireOp",EDGE,"E1.top");var subQ9=sQuery(id+"F0.wireOp",EDGE,"E1.left");var subQ10=sQuery(id+"F0.wireOp",EDGE,"E23.filletArc");var subQ11=sQuery(id+"F0.wireOp",EDGE,"E24.filletArc");Q0=makeQuery(id+"F2.boolean.opBoolean","SPLIT",FACE,{"disambiguationData":[TD([makeQuery(id+"F1.opExtrude","SWEPT_FACE",FACE,{"disambiguationData":[OSD([subQ6])]})])],"derivedFrom":makeQuery(id+"F1.opExtrude","CAP_FACE",FACE,{"disambiguationData":[OSD([subQ6,subQ8,subQ9,subQ7,subQ4,subQ3,subQ2,subQ1,subQ0,subQ5,subQ10,subQ11])],"isStart":true})});}
            var sketch = newSketch(context, id + "F16", { "sketchPlane" : qUnion([Q0])});
            skLineSegment(sketch, "E79.0", {"start": v(-60, 40.3) * mm, "end": v(-60, -40.3) * mm});
            skArc(sketch, "E79.1", {"start": v(56.15, 48.18) * mm, "mid": v(0, 67.5) * mm, "end": v(-56.15, 48.18) * mm});
            skArc(sketch, "E79.2", {"start": v(-56.15, -48.18) * mm, "mid": v(0, -67.5) * mm, "end": v(56.15, -48.18) * mm});
            skLineSegment(sketch, "E79.3", {"start": v(60, 40.3) * mm, "end": v(60, -40.3) * mm});
            skArc(sketch, "E79.4", {"start": v(56.15, -48.18) * mm, "mid": v(58.99, -44.68) * mm, "end": v(60, -40.3) * mm});
            skLineSegment(sketch, "E79.5", {"start": v(-80, -80) * mm, "end": v(-80, 80) * mm});
            skArc(sketch, "E79.6", {"start": v(-56.15, 48.18) * mm, "mid": v(-58.99, 44.68) * mm, "end": v(-60, 40.3) * mm});
            skArc(sketch, "E79.7", {"start": v(-60, -40.3) * mm, "mid": v(-58.99, -44.68) * mm, "end": v(-56.15, -48.18) * mm});
            skArc(sketch, "E79.8", {"start": v(60, 40.3) * mm, "mid": v(58.99, 44.68) * mm, "end": v(56.15, 48.18) * mm});
            skLineSegment(sketch, "E79.9", {"start": v(80, -80) * mm, "end": v(80, 80) * mm});
            skLineSegment(sketch, "E79.10", {"start": v(-70, 90) * mm, "end": v(70, 90) * mm});
            skLineSegment(sketch, "E79.11", {"start": v(-70, -90) * mm, "end": v(70, -90) * mm});
            skArc(sketch, "E79.12", {"start": v(-80, -80) * mm, "mid": v(-77.07, -87.07) * mm, "end": v(-70, -90) * mm});
            skArc(sketch, "E79.13", {"start": v(-70, 90) * mm, "mid": v(-77.07, 87.07) * mm, "end": v(-80, 80) * mm});
            skArc(sketch, "E79.14", {"start": v(80, 80) * mm, "mid": v(77.07, 87.07) * mm, "end": v(70, 90) * mm});
            skArc(sketch, "E79.15", {"start": v(70, -90) * mm, "mid": v(77.07, -87.07) * mm, "end": v(80, -80) * mm});
            skCircle(sketch, "E79.16", {"center": v(60, -67.5) * mm, "radius": 4 * mm});
            skCircle(sketch, "E79.17", {"center": v(60, 67.5) * mm, "radius": 4 * mm});
            skCircle(sketch, "E79.18", {"center": v(-60, 67.5) * mm, "radius": 4 * mm});
            skCircle(sketch, "E79.19", {"center": v(-60, -67.5) * mm, "radius": 4 * mm});
            skLineSegment(sketch, "E80", {"start": v(0, 90) * mm, "end": v(0, 120) * mm, "construction": true});
            skCircle(sketch, "E81", {"center": v(0, 120) * mm, "radius": 6 * mm});
            skArc(sketch, "E82", {"start": v(15, 120) * mm, "mid": v(0, 135) * mm, "end": v(-15, 120) * mm});
            skLineSegment(sketch, "E83", {"start": v(-15, 120) * mm, "end": v(-15, 108) * mm});
            skLineSegment(sketch, "E84", {"start": v(15, 120) * mm, "end": v(15, 108) * mm});
            skLineSegment(sketch, "E85", {"start": v(-15, 108) * mm, "end": v(-33, 90) * mm});
            skLineSegment(sketch, "E86", {"start": v(15, 108) * mm, "end": v(33, 90) * mm});
            skLineSegment(sketch, "E87", {"start": v(-80, 0) * mm, "end": v(80, 0) * mm, "construction": true});
            skLineSegment(sketch, "E88.MirrorCS", {"start": v(15, -108) * mm, "end": v(33, -90) * mm});
            skLineSegment(sketch, "E89.MirrorCS", {"start": v(0, -90) * mm, "end": v(0, -120) * mm, "construction": true});
            skCircle(sketch, "E90.MirrorC", {"center": v(0, -120) * mm, "radius": 6 * mm});
            skLineSegment(sketch, "E91.MirrorCS", {"start": v(15, -120) * mm, "end": v(15, -108) * mm});
            skArc(sketch, "E92.MirrorCS", {"start": v(15, -120) * mm, "mid": v(0, -135) * mm, "end": v(-15, -120) * mm});
            skLineSegment(sketch, "E93.MirrorCS", {"start": v(-15, -120) * mm, "end": v(-15, -108) * mm});
            skLineSegment(sketch, "E94.MirrorCS", {"start": v(-15, -108) * mm, "end": v(-33, -90) * mm});
            skSolve(sketch);
        }
        {
            var Q0;
            Q0 = qSketchRegion(id + "F16", true);
            var Q1;
            Q1=makeQuery(id+"F2.opExtrude","CAP_FACE",FACE,{"disambiguationData":[OSD([sQuery(id+"F0.wireOp",EDGE,"E12"),sQuery(id+"F0.wireOp",EDGE,"E13"),sQuery(id+"F0.wireOp",EDGE,"E14"),sQuery(id+"F0.wireOp",EDGE,"E15"),sQuery(id+"F0.wireOp",EDGE,"E17.filletArc"),sQuery(id+"F0.wireOp",EDGE,"E18.filletArc"),sQuery(id+"F0.wireOp",EDGE,"E19.filletArc"),sQuery(id+"F0.wireOp",EDGE,"E20.filletArc"),sQuery(id+"F0.wireOp",EDGE,"E25.0"),sQuery(id+"F0.wireOp",EDGE,"E25.1"),sQuery(id+"F0.wireOp",EDGE,"E25.2"),sQuery(id+"F0.wireOp",EDGE,"E25.3"),sQuery(id+"F0.wireOp",EDGE,"E25.4"),sQuery(id+"F0.wireOp",EDGE,"E25.5"),sQuery(id+"F0.wireOp",EDGE,"E25.6"),sQuery(id+"F0.wireOp",EDGE,"E25.7")])],"isStart":false});
            extrude(context, id + "F17", {"entities" : qUnion([Q0]), "endBound" : BoundingType.UP_TO_SURFACE, "endBoundEntityFace" : qUnion([Q1]), "depth" : 25 * mm});
        }
    });
